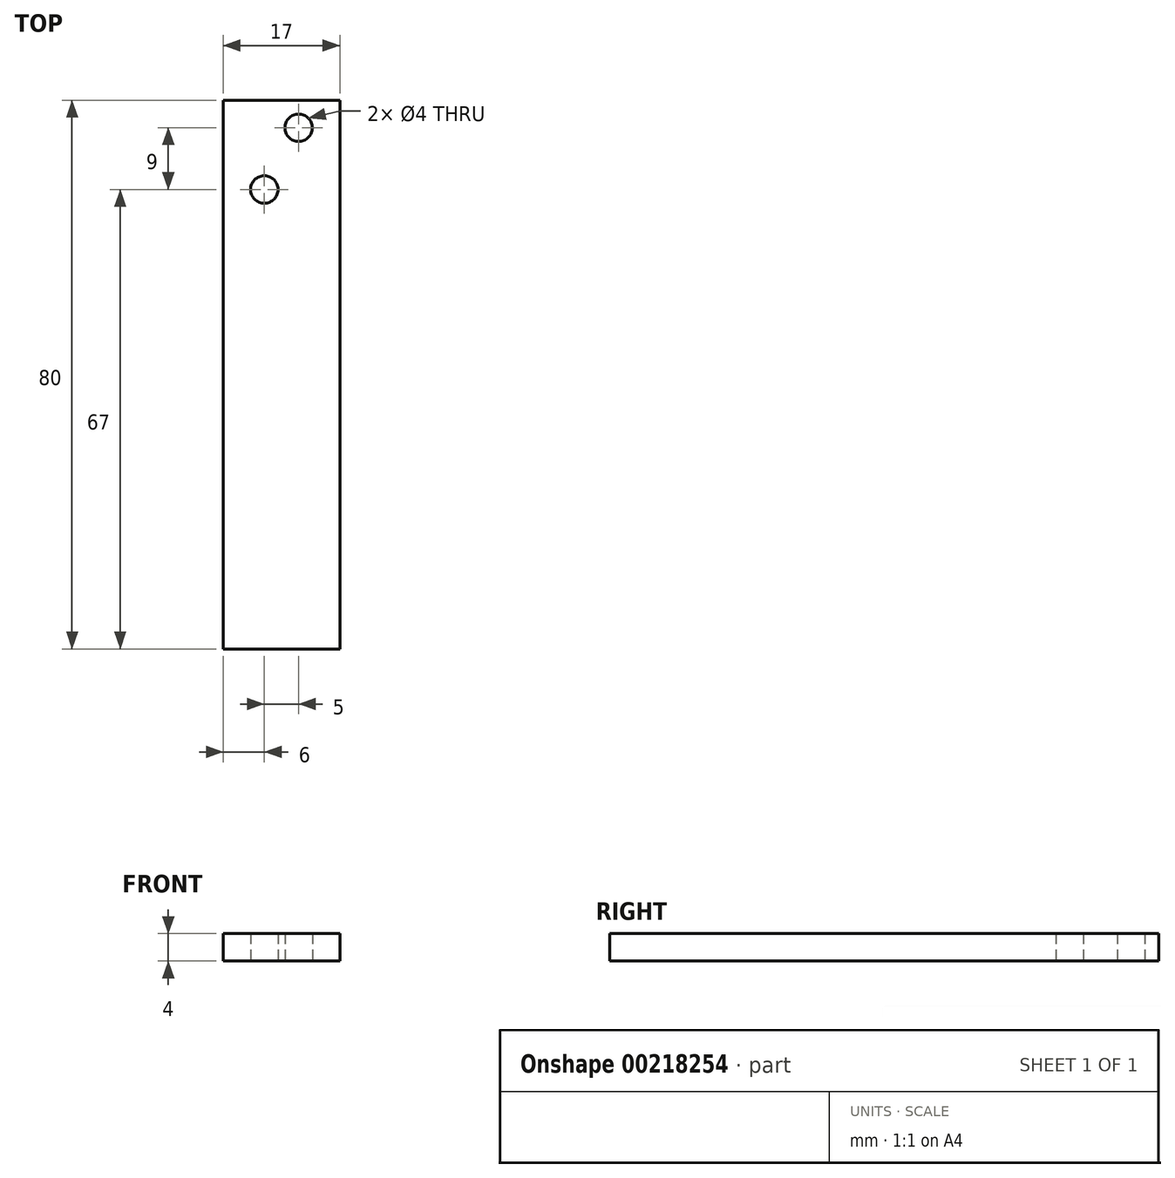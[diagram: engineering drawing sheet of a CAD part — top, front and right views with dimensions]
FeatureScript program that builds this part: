
annotation { "Feature Type Name" : "Feature", "Feature Type Description" : "" }
export const myFeature = defineFeature(function(context is Context, id is Id, definition is map)
    precondition{}
    {
        {
            var Q0;
            Q0=qCreatedBy(makeId("Top.planeOp"),FACE);
            var sketch = newSketch(context, id + "F0", { "sketchPlane" : qUnion([Q0])});
            skLineSegment(sketch, "E0.bottom", {"start": v(0, 0) * mm, "end": v(17, 0) * mm});
            skLineSegment(sketch, "E0.top", {"start": v(0, -80) * mm, "end": v(17, -80) * mm});
            skLineSegment(sketch, "E0.left", {"start": v(0, 0) * mm, "end": v(0, -80) * mm});
            skLineSegment(sketch, "E0.right", {"start": v(17, 0) * mm, "end": v(17, -80) * mm});
            skCircle(sketch, "E1", {"center": v(6, -13) * mm, "radius": 2 * mm});
            skCircle(sketch, "E2", {"center": v(11, -4) * mm, "radius": 2 * mm});
            skSolve(sketch);
        }
        {
            var Q0;
            Q0 = qSketchRegion(id + "F0", true);
            extrude(context, id + "F1", {"entities" : qUnion([Q0]), "depth" : 4 * mm});
        }
    });
